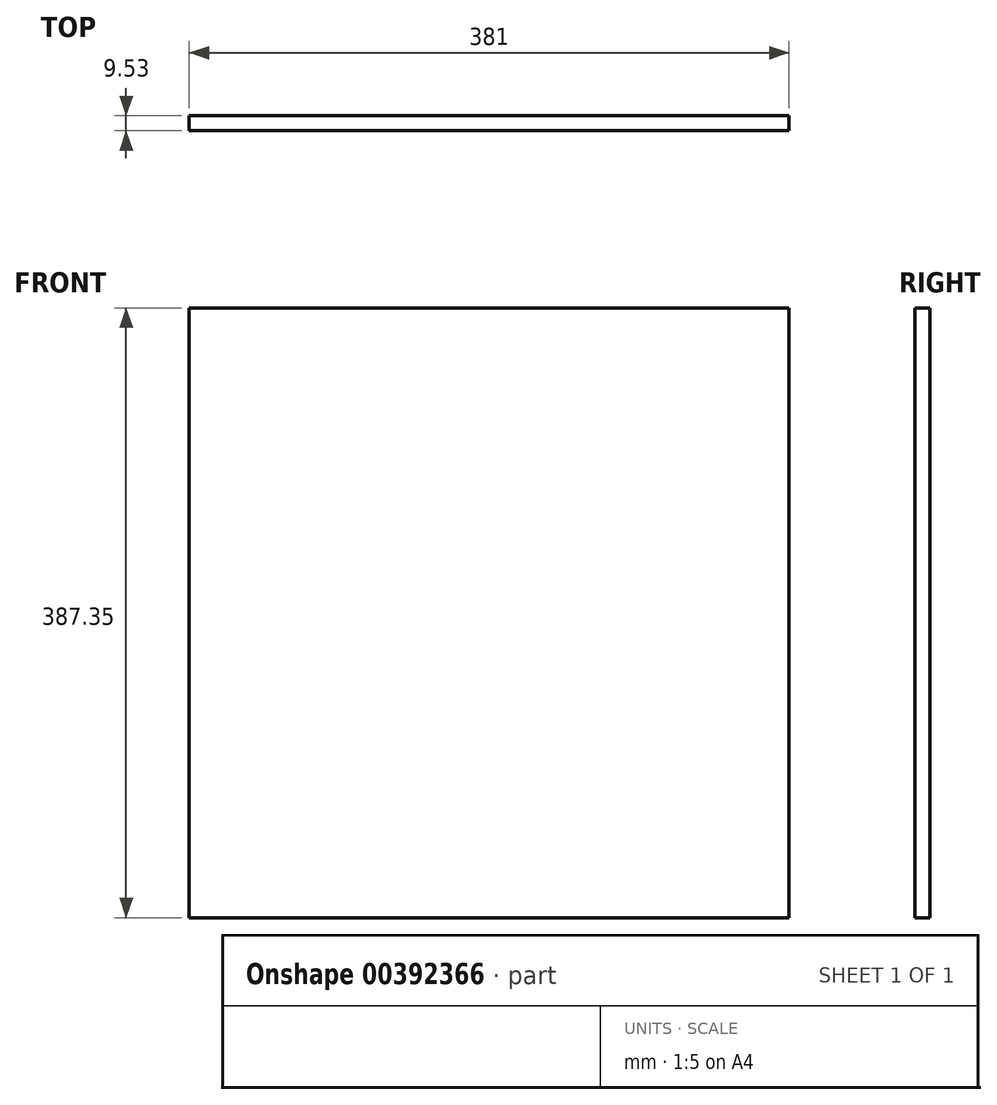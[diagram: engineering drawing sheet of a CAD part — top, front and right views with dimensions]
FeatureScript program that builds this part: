
annotation { "Feature Type Name" : "Feature", "Feature Type Description" : "" }
export const myFeature = defineFeature(function(context is Context, id is Id, definition is map)
    precondition{}
    {
        {
            var Q0;
            Q0=qCreatedBy(makeId("Front.planeOp"),FACE);
            var sketch = newSketch(context, id + "F0", { "sketchPlane" : qUnion([Q0])});
            skLineSegment(sketch, "E0.bottom", {"start": v(-190.5, 0) * mm, "end": v(190.5, 0) * mm});
            skLineSegment(sketch, "E0.top", {"start": v(-190.5, -387.35) * mm, "end": v(190.5, -387.35) * mm});
            skLineSegment(sketch, "E0.left", {"start": v(-190.5, 0) * mm, "end": v(-190.5, -387.35) * mm});
            skLineSegment(sketch, "E0.right", {"start": v(190.5, 0) * mm, "end": v(190.5, -387.35) * mm});
            skSolve(sketch);
        }
        {
            var Q0;
            Q0=makeQuery(id+"F0.imprint","IMPRINT",FACE,{"disambiguationData":[TD([[makeQuery(id+"F0.imprint","IMPRINT",EDGE,{"derivedFrom":sQuery(id+"F0.wireOp",EDGE,"E0.bottom")}),-1.0]])]});
            extrude(context, id + "F1", {"entities" : qUnion([Q0]), "depth" : 9.52 * mm});
        }
    });
